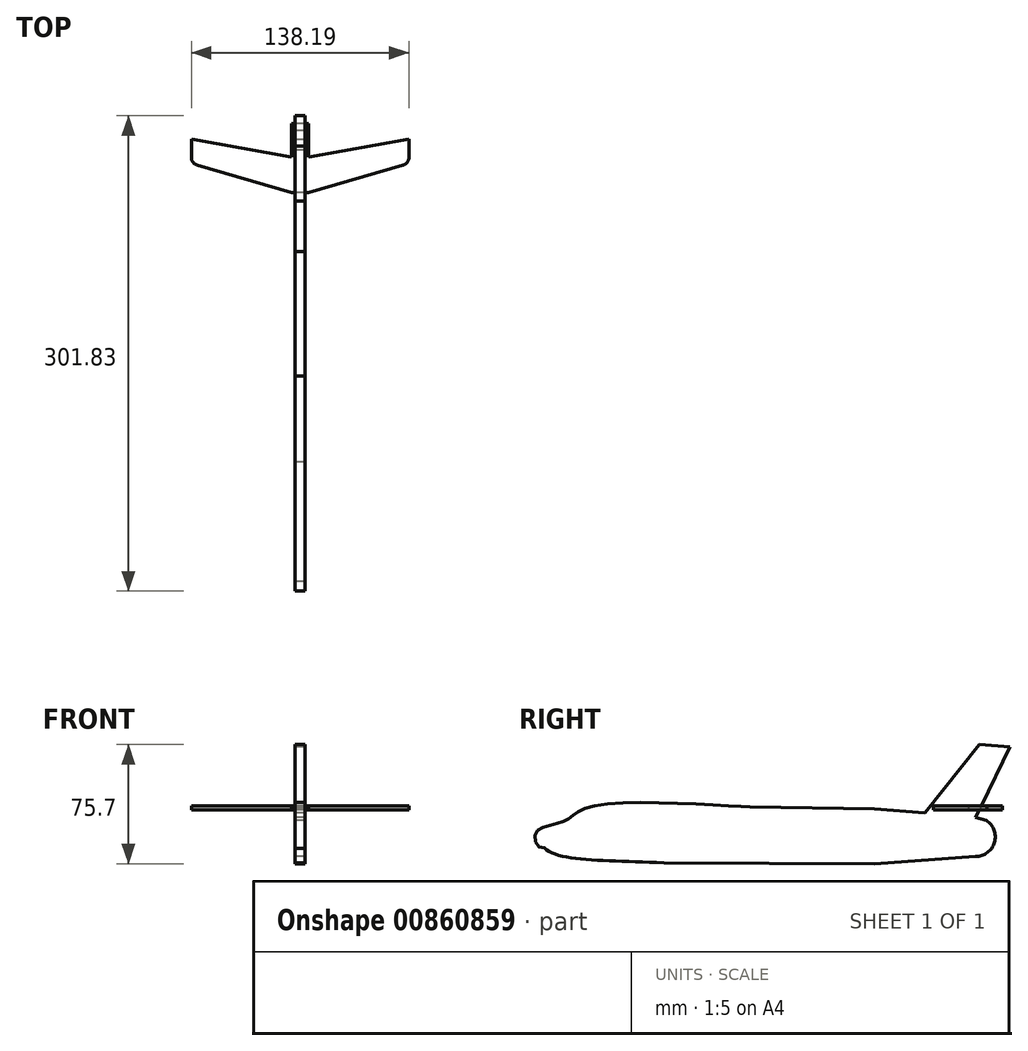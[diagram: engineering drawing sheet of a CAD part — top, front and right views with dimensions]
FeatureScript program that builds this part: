
annotation { "Feature Type Name" : "Feature", "Feature Type Description" : "" }
export const myFeature = defineFeature(function(context is Context, id is Id, definition is map)
    precondition{}
    {
        {
            var Q0;
            Q0=qCreatedBy(makeId("Right.planeOp"),FACE);
            var sketch = newSketch(context, id + "F0", { "sketchPlane" : qUnion([Q0])});
            skLineSegment(sketch, "E0", {"start": v(-2.58, 31.24) * mm, "end": v(76.3, 30.07) * mm});
            skLineSegment(sketch, "E1", {"start": v(-57.43, -4.27) * mm, "end": v(76.3, -4.8) * mm});
            skPoint(sketch, "E2.center.orphan", {"position": v(119.57, 10.9) * mm});
            skPoint(sketch, "E3.end.orphan", {"position": v(119.57, 12.24) * mm});
            skArc(sketch, "E4", {"start": v(140.63, -0.27) * mm, "mid": v(153.13, 12.24) * mm, "end": v(140.63, 24.75) * mm});
            skLineSegment(sketch, "E5", {"start": v(140.63, -0.27) * mm, "end": v(76.3, -4.8) * mm});
            skLineSegment(sketch, "E6", {"start": v(108.47, 27.4) * mm, "end": v(76.3, 30.07) * mm});
            skLineSegment(sketch, "E7", {"start": v(108.47, 27.4) * mm, "end": v(143.18, 70.9) * mm});
            skLineSegment(sketch, "E8", {"start": v(143.18, 70.9) * mm, "end": v(162.54, 69.3) * mm});
            skLineSegment(sketch, "E9", {"start": v(162.54, 69.3) * mm, "end": v(140.63, 24.75) * mm});
            skPoint(sketch, "E10.orphan", {"position": v(90.64, 39.36) * mm});
            skPoint(sketch, "E11.orphan", {"position": v(95.68, 56.17) * mm});
            skPoint(sketch, "E12.start.orphan", {"position": v(124.53, 47.52) * mm});
            skPoint(sketch, "E13.start.orphan", {"position": v(110.1, 51.85) * mm});
            skPoint(sketch, "E14.start.orphan", {"position": v(99.55, 33.38) * mm});
            skLineSegment(sketch, "E15", {"start": v(162.54, 69.3) * mm, "end": v(178.9, 40.45) * mm});
            skLineSegment(sketch, "E16", {"start": v(178.9, 40.45) * mm, "end": v(166.1, 17.2) * mm});
            skLineSegment(sketch, "E17", {"start": v(166.1, 17.2) * mm, "end": v(140.63, 24.75) * mm});
            skPoint(sketch, "E18.end.orphan", {"position": v(95.68, -31.88) * mm});
            skPoint(sketch, "E18.start.orphan", {"position": v(76.3, -28.47) * mm});
            skPoint(sketch, "E19.1.internal.orphan", {"position": v(-92.65, -2.36) * mm});
            skFitSpline(sketch, "E20", {"points": [v(-57.43, -4.27) * mm, v(-133.08, 5.12) * mm], "startDerivative": vector(-105.66, 5.75) * mm, "endDerivative": vector(-27.36, 27.36) * mm});
            skFitSpline(sketch, "E21", {"points": [v(-2.58, 31.24) * mm, v(-104.8, 31.24) * mm, v(-121.23, 21.89) * mm, v(-138.64, 14.74) * mm, v(-133.08, 5.12) * mm], "startDerivative": vector(-107.53, 4.18) * mm, "endDerivative": vector(102.18, 21.9) * mm});
            skSolve(sketch);
        }
        {
            var Q0;
            Q0=makeQuery(id+"F0.imprint","IMPRINT",FACE,{"disambiguationData":[TD([[makeQuery(id+"F0.imprint","IMPRINT",EDGE,{"derivedFrom":sQuery(id+"F0.wireOp",EDGE,"KEdVg5Xh-iTQH-8Z5K-S9Iy-x4rNJ19G54fd")}),1.0]])]});
            var Q1;
            {var subQ2=sQuery(id+"F0.wireOp",EDGE,"E12");Q1=makeQuery(id+"F0.imprint","IMPRINT",FACE,{"disambiguationData":[TD([[makeQuery(id+"F0.imprint","IMPRINT",EDGE,{"derivedFrom":subQ2}),1.0]])]});}
            var Q2;
            Q2=makeQuery(id+"F0.imprint","IMPRINT",FACE,{"disambiguationData":[TD([[makeQuery(id+"F0.imprint","IMPRINT",EDGE,{"derivedFrom":sQuery(id+"F0.wireOp",EDGE,"VLLXbdth-bKSb-qAgS-ZZtV-Ev8Pa3ZnHSMD.bottom")}),-1.0]])]});
            var Q3;
            Q3=makeQuery(id+"F0.imprint","IMPRINT",FACE,{"disambiguationData":[TD([[makeQuery(id+"F0.imprint","IMPRINT",EDGE,{"derivedFrom":sQuery(id+"F0.wireOp",EDGE,"E0")}),-1.0]])]});
            extrude(context, id + "F1", {"entities" : qUnion([Q0, Q1, Q2, Q3]), "depth" : 6.35 * mm, "offsetDistance" : 25.4 * mm});
        }
        {
            var Q0;
            Q0=qCreatedBy(makeId("Right.planeOp"),FACE);
            var sketch = newSketch(context, id + "F2", { "sketchPlane" : qUnion([Q0])});
            skLineSegment(sketch, "E22", {"start": v(113.7, 32) * mm, "end": v(157.6, 32) * mm});
            skLineSegment(sketch, "E23", {"start": v(157.6, 32) * mm, "end": v(157.6, 29.46) * mm});
            skLineSegment(sketch, "E24", {"start": v(157.6, 29.46) * mm, "end": v(113.7, 29.46) * mm});
            skLineSegment(sketch, "E25", {"start": v(113.7, 29.46) * mm, "end": v(113.7, 32) * mm});
            skPoint(sketch, "E26.end.orphan", {"position": v(154.34, 12.82) * mm});
            skPoint(sketch, "E26.start.orphan", {"position": v(154.34, 10.97) * mm});
            skSolve(sketch);
        }
        {
            var Q0;
            Q0 = qSketchRegion(id + "F2", true);
            extrude(context, id + "F3", {"entities" : qUnion([Q0]), "endBound" : BoundingType.SYMMETRIC, "depth" : 264.16 * mm, "offsetDistance" : 25.4 * mm});
        }
        {
            var Q0;
            Q0=makeQuery(id+"F3.opExtrude","SWEPT_FACE",FACE,{"disambiguationData":[OSD([sQuery(id+"F2.wireOp",EDGE,"E22")])]});
            var sketch = newSketch(context, id + "F4", { "sketchPlane" : qUnion([Q0])});
            skLineSegment(sketch, "E27", {"start": v(8.57, 113.7) * mm, "end": v(68.62, 131.25) * mm});
            skLineSegment(sketch, "E28", {"start": v(72.27, 136.13) * mm, "end": v(72.27, 147.69) * mm});
            skLineSegment(sketch, "E29", {"start": v(72.27, 147.69) * mm, "end": v(8.57, 136.28) * mm});
            skLineSegment(sketch, "E30", {"start": v(8.57, 136.28) * mm, "end": v(8.57, 160.4) * mm});
            skLineSegment(sketch, "E31", {"start": v(8.57, 160.4) * mm, "end": v(142.12, 164.67) * mm});
            skLineSegment(sketch, "E32", {"start": v(142.12, 164.67) * mm, "end": v(138.46, 103.69) * mm});
            skLineSegment(sketch, "E33", {"start": v(138.46, 103.69) * mm, "end": v(11.15, 106.69) * mm});
            skLineSegment(sketch, "E34", {"start": v(11.15, 106.69) * mm, "end": v(8.57, 113.7) * mm});
            skPoint(sketch, "E35.visualSharp", {"position": v(72.27, 132.32) * mm});
            skArc(sketch, "E35.filletArc", {"start": v(68.62, 131.25) * mm, "mid": v(71.26, 133.08) * mm, "end": v(72.27, 136.13) * mm});
            skPoint(sketch, "E36.0", {"position": v(3.17, 162.54) * mm});
            skLineSegment(sketch, "E37", {"start": v(3.17, 162.54) * mm, "end": v(3.17, 174.76) * mm, "construction": true});
            skLineSegment(sketch, "E38.MirrorCS", {"start": v(-2.22, 136.28) * mm, "end": v(-2.22, 160.4) * mm});
            skLineSegment(sketch, "E39.MirrorCS", {"start": v(-65.92, 147.69) * mm, "end": v(-2.22, 136.28) * mm});
            skLineSegment(sketch, "E40.MirrorCS", {"start": v(-65.92, 136.13) * mm, "end": v(-65.92, 147.69) * mm});
            skArc(sketch, "E41.MirrorCS", {"start": v(-62.27, 131.25) * mm, "mid": v(-64.9, 133.08) * mm, "end": v(-65.92, 136.13) * mm});
            skLineSegment(sketch, "E42.MirrorCS", {"start": v(-2.22, 113.7) * mm, "end": v(-62.27, 131.25) * mm});
            skLineSegment(sketch, "E43.MirrorCS", {"start": v(-4.8, 106.69) * mm, "end": v(-2.22, 113.7) * mm});
            skLineSegment(sketch, "E44.MirrorCS", {"start": v(-132.1, 103.69) * mm, "end": v(-4.8, 106.69) * mm});
            skLineSegment(sketch, "E45.MirrorCS", {"start": v(-2.22, 160.4) * mm, "end": v(-135.77, 164.67) * mm});
            skLineSegment(sketch, "E46.MirrorCS", {"start": v(-135.77, 164.67) * mm, "end": v(-132.1, 103.69) * mm});
            skSolve(sketch);
        }
        {
            var Q0;
            Q0 = qSketchRegion(id + "F4", true);
            extrude(context, id + "F5", {"entities" : qUnion([Q0]), "operationType" : NewBodyOperationType.REMOVE, "oppositeDirection" : true, "depth" : 25.4 * mm, "offsetDistance" : 25.4 * mm});
        }
    });
